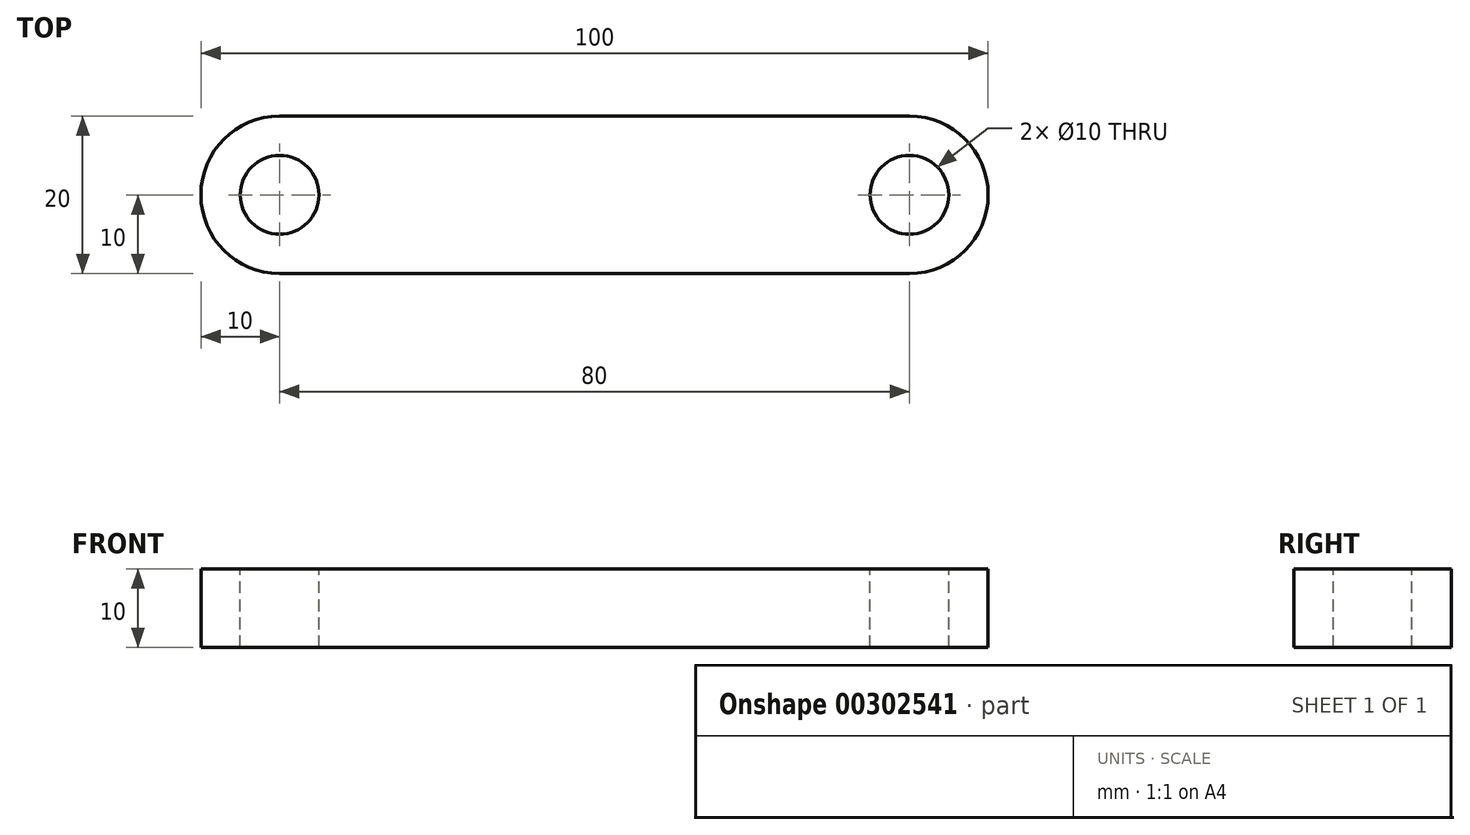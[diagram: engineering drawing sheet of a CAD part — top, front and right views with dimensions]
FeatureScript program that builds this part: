
annotation { "Feature Type Name" : "Feature", "Feature Type Description" : "" }
export const myFeature = defineFeature(function(context is Context, id is Id, definition is map)
    precondition{}
    {
        {
            var Q0;
            Q0=qCreatedBy(makeId("Top.planeOp"),FACE);
            var sketch = newSketch(context, id + "F0", { "sketchPlane" : qUnion([Q0])});
            skLineSegment(sketch, "E0.bottom", {"start": v(0, 0) * mm, "end": v(80, 0) * mm});
            skLineSegment(sketch, "E0.top", {"start": v(0, 20) * mm, "end": v(80, 20) * mm});
            skArc(sketch, "E1", {"start": v(0, 20) * mm, "mid": v(-10, 10) * mm, "end": v(0, 0) * mm});
            skArc(sketch, "E2", {"start": v(80, 0) * mm, "mid": v(90, 10) * mm, "end": v(80, 20) * mm});
            skCircle(sketch, "E3", {"center": v(0, 10) * mm, "radius": 5 * mm});
            skCircle(sketch, "E4", {"center": v(80, 10) * mm, "radius": 5 * mm});
            skSolve(sketch);
        }
        {
            var Q0;
            Q0=makeQuery(id+"F0.imprint","IMPRINT",FACE,{"disambiguationData":[TD([[makeQuery(id+"F0.imprint","IMPRINT",EDGE,{"derivedFrom":sQuery(id+"F0.wireOp",EDGE,"E0.bottom")}),1.0]])]});
            extrude(context, id + "F1", {"entities" : qUnion([Q0]), "oppositeDirection" : true, "depth" : 10 * mm});
        }
    });
